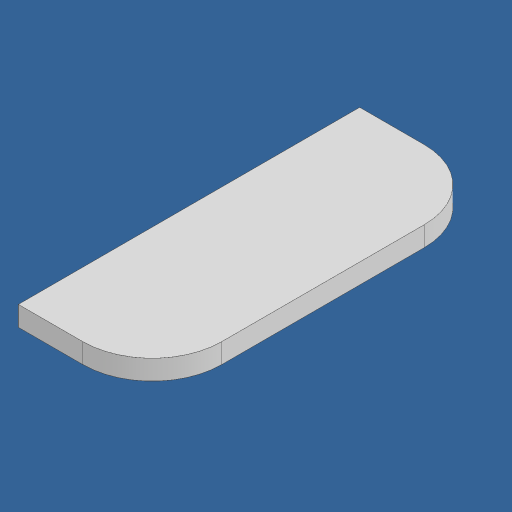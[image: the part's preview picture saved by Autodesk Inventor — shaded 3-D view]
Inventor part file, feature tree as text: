
AUTODESK INVENTOR PART (.ipt)
format: ipt  version: 2024.2 (Build 282272000, 272)  size: 87,552 bytes
history: native  units: mm
features: extrude x1, fillet x1, sketch x1
ambient origin geometry x8: Origin, YZ Plane, XZ Plane, XY Plane, X Axis, Y Axis, Z Axis, Center Point
bodies: Solid1 (feature_tree)
feature tree (3):
  extrude  "Extrusion1"  Depth=13.5mm
  fillet  "Fillet1"  Radius=2.0mm
  sketch  "Sketch1"  dims[d0=34.4mm d1=13.5mm d2=2.0mm d3=0.0mm d4=7.0mm]
